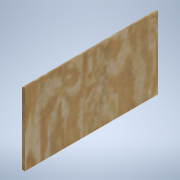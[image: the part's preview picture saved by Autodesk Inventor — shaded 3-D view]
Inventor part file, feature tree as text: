
AUTODESK INVENTOR PART (.ipt)
format: ipt  version: 2021.1 (Build 251245000, 245)  size: 120,832 bytes
history: native  units: in
note: dims shown in document units (in); Inventor stores cm internally (conversion verified against a paired STEP export)
features: reference x4, other x4, extrude x1, sketch x1
ambient origin geometry x8: Origin, YZ Plane, XZ Plane, XY Plane, X Axis, Y Axis, Z Axis, Center Point
bodies: Solid1 (feature_tree)
feature tree (10):
  extrude  "Extrusion1"  [1 undecoded]
  sketch  "Sketch1"  dims[d1=10.6299in d2=0.0in]
  reference  "Reference1"
  reference  "Reference2"
  reference  "Reference3"
  reference  "Reference4"
  other  "<userpath>\Documents\Kerbal Kontroller\Design\Final\Inventor\Final.iam"
  other  "Final.iam"
  other  "Sides:1"
  other  "Bottom:1"
note: 1 required parameter value undecoded (feature->parameter linkage not recoverable at this tier; creation-order binding heuristic only, values carry confidence <= 0.55)
